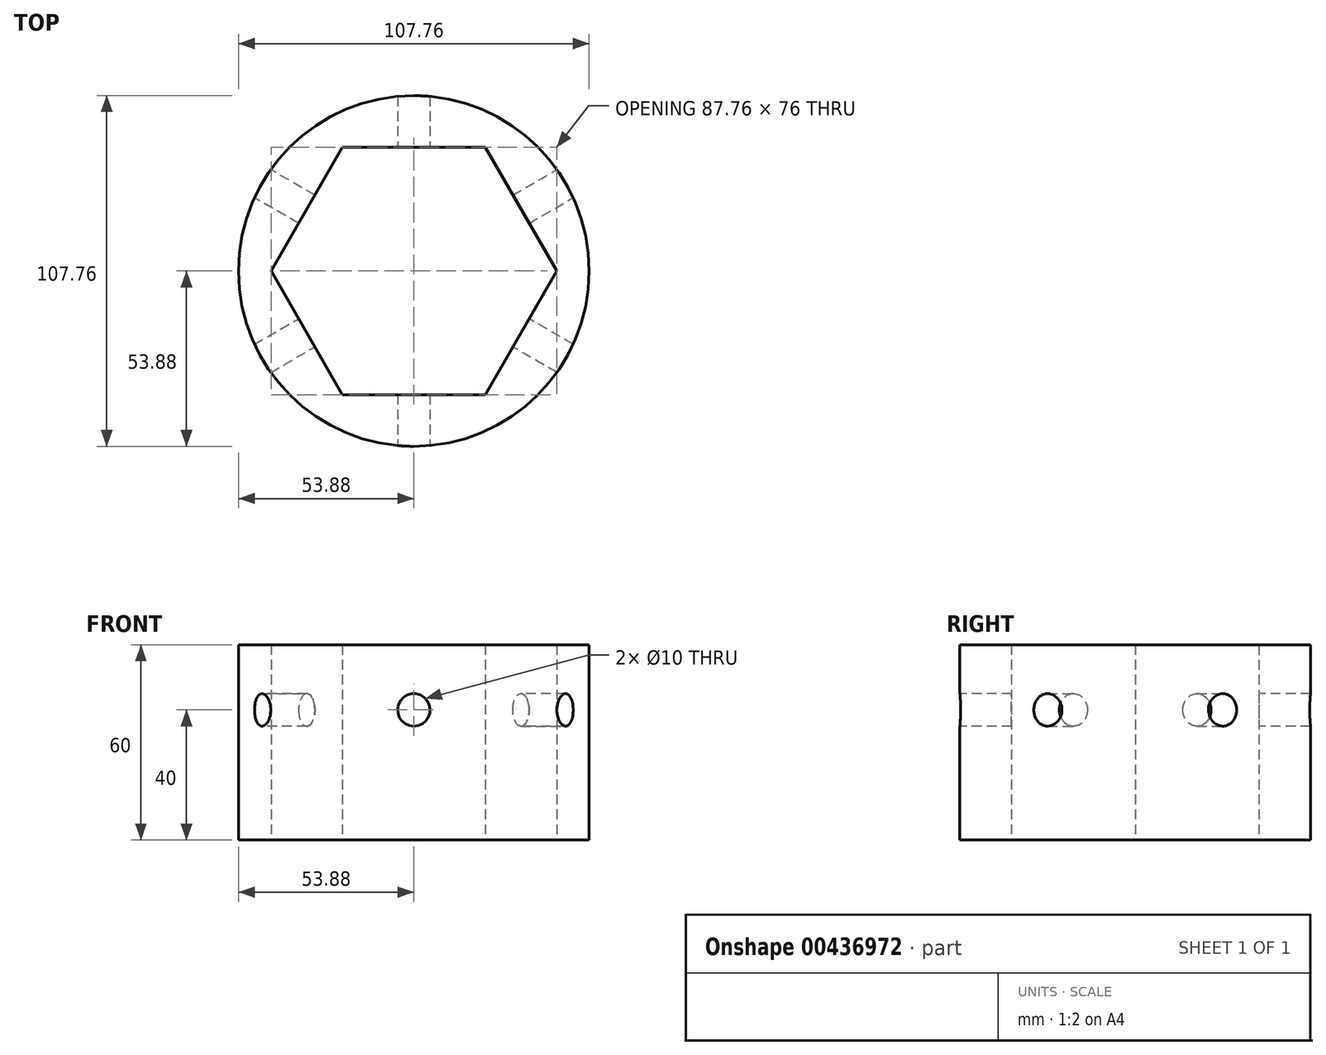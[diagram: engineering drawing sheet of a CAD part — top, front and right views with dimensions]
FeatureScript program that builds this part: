
annotation { "Feature Type Name" : "Feature", "Feature Type Description" : "" }
export const myFeature = defineFeature(function(context is Context, id is Id, definition is map)
    precondition{}
    {
        {
            var Q0;
            Q0=qCreatedBy(makeId("Top.planeOp"),FACE);
            var sketch = newSketch(context, id + "F0", { "sketchPlane" : qUnion([Q0])});
            skCircle(sketch, "E0", {"center": v(0, 0) * mm, "radius": 38 * mm});
            skCircle(sketch, "E1.cCircle", {"center": v(0, 0) * mm, "radius": 38 * mm, "construction": true});
            skLineSegment(sketch, "E1.0", {"start": v(-21.94, 38) * mm, "end": v(21.94, 38) * mm});
            skLineSegment(sketch, "E1.1", {"start": v(21.94, 38) * mm, "end": v(43.88, 0) * mm});
            skLineSegment(sketch, "E1.2", {"start": v(43.88, 0) * mm, "end": v(21.94, -38) * mm});
            skLineSegment(sketch, "E1.3", {"start": v(21.94, -38) * mm, "end": v(-21.94, -38) * mm});
            skLineSegment(sketch, "E1.4", {"start": v(-21.94, -38) * mm, "end": v(-43.88, 0) * mm});
            skLineSegment(sketch, "E1.5", {"start": v(-43.88, 0) * mm, "end": v(-21.94, 38) * mm});
            skPoint(sketch, "E1.0.midPoint", {"position": v(0, 38) * mm});
            skCircle(sketch, "E2", {"center": v(0, 0) * mm, "radius": 53.88 * mm});
            skSolve(sketch);
        }
        {
            var Q0;
            Q0 = qSketchRegion(id + "F0", true);
            extrude(context, id + "F1", {"entities" : qUnion([Q0]), "depth" : 10 * mm});
        }
        {
            var Q0;
            Q0 = qSketchRegion(id + "F0", true);
            extrude(context, id + "F2", {"entities" : qUnion([Q0]), "operationType" : NewBodyOperationType.ADD, "depth" : 60 * mm});
        }
        {
            var Q0;
            Q0=qCreatedBy(makeId("Front.planeOp"),FACE);
            var sketch = newSketch(context, id + "F3", { "sketchPlane" : qUnion([Q0])});
            skCircle(sketch, "E3", {"center": v(0, 40) * mm, "radius": 5 * mm});
            skSolve(sketch);
        }
        {
            var Q0;
            Q0 = qSketchRegion(id + "F3", true);
            extrude(context, id + "F4", {"entities" : qUnion([Q0]), "operationType" : NewBodyOperationType.REMOVE, "endBound" : BoundingType.THROUGH_ALL, "oppositeDirection" : true, "depth" : 87.7 * mm, "hasSecondDirection" : true, "secondDirectionBound" : SecondDirectionBoundingType.THROUGH_ALL, "secondDirectionOppositeDirection" : false, "secondDirectionDepth" : 25 * mm});
        }
        {
            var Q0;
            {var subQ0=sQuery(id+"F0.wireOp",EDGE,"E1.2");Q0=makeQuery(id+"F2.boolean.opBoolean","MERGE",FACE,{"derivedFrom":[makeQuery(id+"F1.opExtrude","SWEPT_FACE",FACE,{"disambiguationData":[OSD([subQ0])]}),makeQuery(id+"F2.opExtrude","SWEPT_FACE",FACE,{"disambiguationData":[OSD([subQ0])]})]});}
            cPlane(context, id + "F5", {"entities" : qUnion([Q0]), "cplaneType" : CPlaneType.OFFSET, "offset" : 37.5 * mm, "width" : 150 * mm, "height" : 150 * mm});
        }
        {
            var Q0;
            Q0=qCreatedBy(id+"F5.planeOp",FACE);
            var sketch = newSketch(context, id + "F6", { "sketchPlane" : qUnion([Q0])});
            skCircle(sketch, "E4", {"center": v(0, 40) * mm, "radius": 5 * mm});
            skSolve(sketch);
        }
        {
            var Q0;
            Q0 = qSketchRegion(id + "F6", true);
            extrude(context, id + "F7", {"entities" : qUnion([Q0]), "operationType" : NewBodyOperationType.REMOVE, "endBound" : BoundingType.THROUGH_ALL, "oppositeDirection" : true, "depth" : 25 * mm, "hasSecondDirection" : true, "secondDirectionBound" : SecondDirectionBoundingType.THROUGH_ALL, "secondDirectionOppositeDirection" : false, "secondDirectionDepth" : 25 * mm});
        }
        {
            var Q0;
            {var subQ0=sQuery(id+"F0.wireOp",EDGE,"E1.1");Q0=makeQuery(id+"F2.boolean.opBoolean","MERGE",FACE,{"derivedFrom":[makeQuery(id+"F1.opExtrude","SWEPT_FACE",FACE,{"disambiguationData":[OSD([subQ0])]}),makeQuery(id+"F2.opExtrude","SWEPT_FACE",FACE,{"disambiguationData":[OSD([subQ0])]})]});}
            cPlane(context, id + "F8", {"entities" : qUnion([Q0]), "cplaneType" : CPlaneType.OFFSET, "offset" : 37.5 * mm, "width" : 150 * mm, "height" : 150 * mm});
        }
        {
            var Q0;
            Q0=qCreatedBy(id+"F8.planeOp",FACE);
            var sketch = newSketch(context, id + "F9", { "sketchPlane" : qUnion([Q0])});
            skCircle(sketch, "E5", {"center": v(0, 40) * mm, "radius": 5 * mm});
            skSolve(sketch);
        }
        {
            var Q0;
            Q0 = qSketchRegion(id + "F9", true);
            extrude(context, id + "F10", {"entities" : qUnion([Q0]), "operationType" : NewBodyOperationType.REMOVE, "endBound" : BoundingType.THROUGH_ALL, "depth" : 25 * mm, "hasSecondDirection" : true, "secondDirectionBound" : SecondDirectionBoundingType.THROUGH_ALL, "secondDirectionOppositeDirection" : true, "secondDirectionDepth" : 25 * mm});
        }
    });
